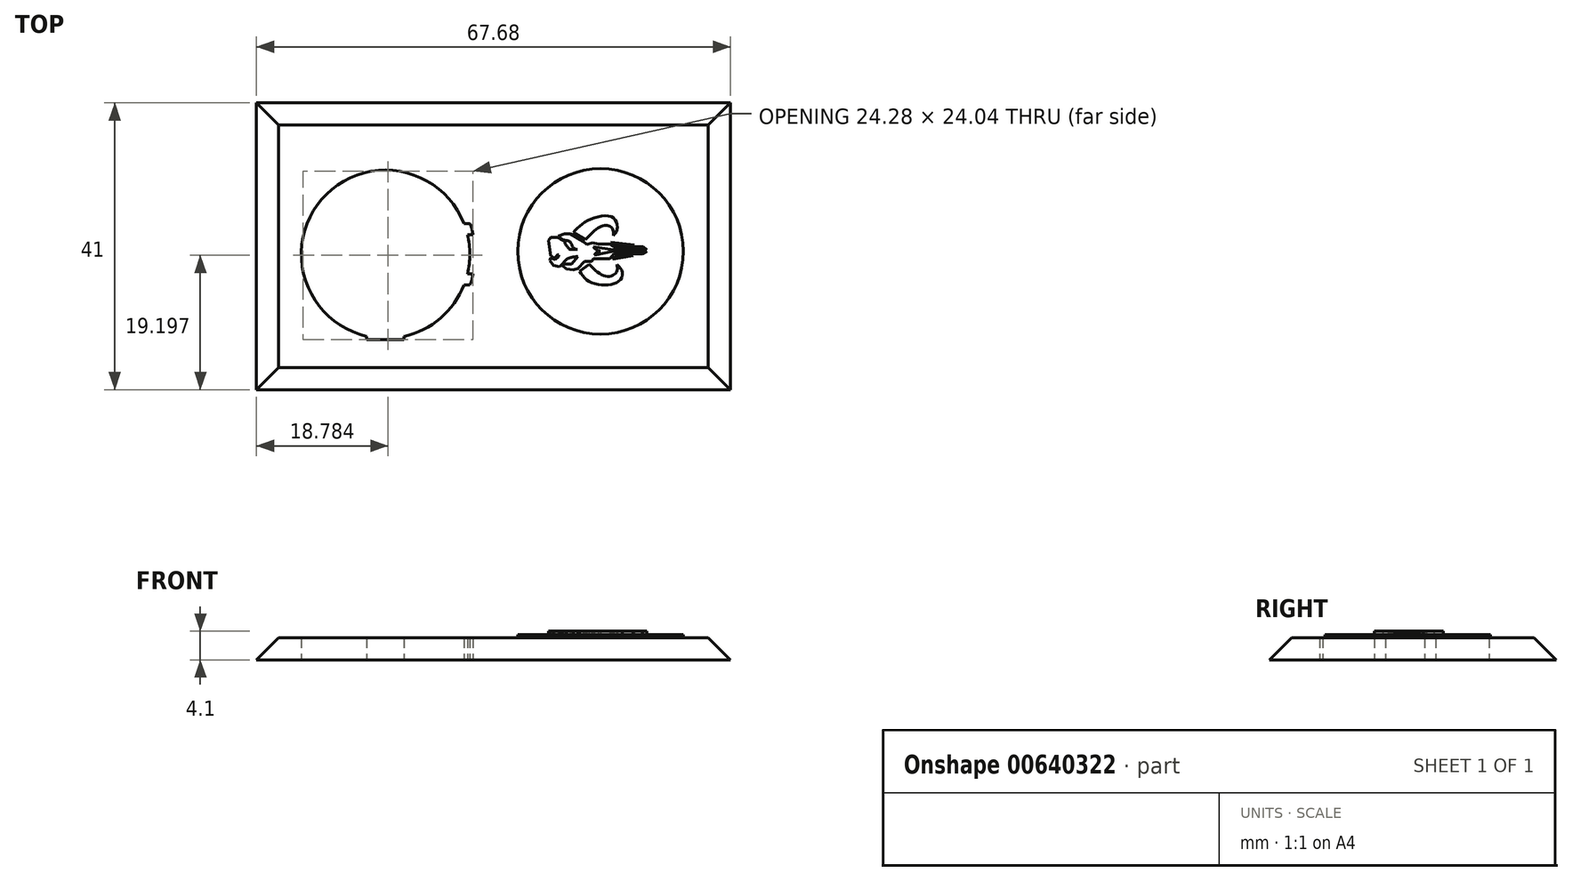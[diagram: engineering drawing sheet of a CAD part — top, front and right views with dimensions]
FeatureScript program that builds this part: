
annotation { "Feature Type Name" : "Feature", "Feature Type Description" : "" }
export const myFeature = defineFeature(function(context is Context, id is Id, definition is map)
    precondition{}
    {
        {
            var Q0;
            Q0=qCreatedBy(makeId("Top.planeOp"),FACE);
            var sketch = newSketch(context, id + "F0", { "sketchPlane" : qUnion([Q0])});
            skArc(sketch, "E0", {"start": v(2.63, -11.74) * mm, "mid": v(7.83, -9.13) * mm, "end": v(11.2, -4.38) * mm});
            skLineSegment(sketch, "E1.top", {"start": v(-2.68, -12.18) * mm, "end": v(2.63, -12.18) * mm});
            skLineSegment(sketch, "E1.left", {"start": v(-2.68, -11.73) * mm, "end": v(-2.68, -12.18) * mm});
            skLineSegment(sketch, "E1.right", {"start": v(2.63, -11.74) * mm, "end": v(2.63, -12.18) * mm});
            skArc(sketch, "E2", {"start": v(12.05, -4.38) * mm, "mid": v(12.31, -3.6) * mm, "end": v(12.49, -2.79) * mm});
            skLineSegment(sketch, "E3", {"start": v(12.05, -4.38) * mm, "end": v(11.2, -4.38) * mm});
            skLineSegment(sketch, "E4", {"start": v(12.49, -2.79) * mm, "end": v(11.7, -2.79) * mm});
            skArc(sketch, "E5.trimOffspring", {"start": v(11.7, -2.79) * mm, "mid": v(12.03, 0) * mm, "end": v(11.7, 2.79) * mm});
            skLineSegment(sketch, "E6.MirrorCS", {"start": v(12.05, 4.38) * mm, "end": v(11.2, 4.38) * mm});
            skLineSegment(sketch, "E7.MirrorCS", {"start": v(12.49, 2.79) * mm, "end": v(11.7, 2.79) * mm});
            skArc(sketch, "E8.MirrorCS", {"start": v(12.05, 4.38) * mm, "mid": v(12.31, 3.6) * mm, "end": v(12.49, 2.79) * mm});
            skArc(sketch, "E9.trimOffspring", {"start": v(11.2, 4.38) * mm, "mid": v(-9.11, 7.85) * mm, "end": v(-2.68, -11.73) * mm});
            skLineSegment(sketch, "E10.bottom", {"start": v(-18.44, -19.36) * mm, "end": v(49.24, -19.36) * mm});
            skLineSegment(sketch, "E10.top", {"start": v(-18.44, 21.64) * mm, "end": v(49.24, 21.64) * mm});
            skLineSegment(sketch, "E10.left", {"start": v(-18.44, -19.36) * mm, "end": v(-18.44, 21.64) * mm});
            skLineSegment(sketch, "E10.right", {"start": v(49.24, -19.36) * mm, "end": v(49.24, 21.64) * mm});
            skSolve(sketch);
        }
        {
            var Q0;
            Q0=makeQuery(id+"F0.imprint","IMPRINT",FACE,{"disambiguationData":[TD([[makeQuery(id+"F0.imprint","IMPRINT",EDGE,{"derivedFrom":sQuery(id+"F0.wireOp",EDGE,"E0")}),-1.0]])]});
            extrude(context, id + "F1", {"entities" : qUnion([Q0]), "depth" : 3.17 * mm, "offsetDistance" : 25 * mm});
        }
        {
            var Q0;
            Q0=makeQuery(id+"F0.imprint","IMPRINT",FACE,{"disambiguationData":[TD([[makeQuery(id+"F0.imprint","IMPRINT",EDGE,{"derivedFrom":sQuery(id+"F0.wireOp",EDGE,"E0")}),1.0]])]});
            extrude(context, id + "F2", {"entities" : qUnion([Q0]), "depth" : 1 / 406.4 * mm, "offsetDistance" : 25 * mm});
        }
        {
            var Q0;
            Q0=qCreatedBy(makeId("Top.planeOp"),FACE);
            var sketch = newSketch(context, id + "F3", { "sketchPlane" : qUnion([Q0])});
            skCircle(sketch, "E11", {"center": v(30.7, 0.41) * mm, "radius": 11.82 * mm});
            skPoint(sketch, "E11.first.point", {"position": v(42.5, 0.04) * mm});
            skPoint(sketch, "E11.second.point", {"position": v(18.88, 0.85) * mm});
            skPoint(sketch, "E11.third.point", {"position": v(31.83, 12.18) * mm});
            skFitSpline(sketch, "E12", {"points": [v(27.7, -2.4) * mm, v(28.93, -3.83) * mm, v(31.38, -4.38) * mm, v(33.21, -3.9) * mm, v(33.83, -2.68) * mm, v(33.01, -1.45) * mm], "startDerivative": vector(4.86, -7.94) * mm, "endDerivative": vector(-6.38, 6.46) * mm});
            skFitSpline(sketch, "E13", {"points": [v(33.01, -1.45) * mm, v(33.01, -2.47) * mm, v(31.99, -3.15) * mm, v(30.15, -2.47) * mm, v(29.06, -1.45) * mm, v(29, -1.45) * mm], "startDerivative": vector(1.04, -5.28) * mm, "endDerivative": vector(-1.05, -0.42) * mm});
            skLineSegment(sketch, "E14", {"start": v(27.7, -2.4) * mm, "end": v(29.01, -1.44) * mm});
            skFitSpline(sketch, "E15", {"points": [v(25.8, 1.98) * mm, v(26.37, 1.74) * mm, v(26.8, 0.94) * mm, v(27.4, 0.67) * mm], "startDerivative": vector(2.1, -0.35) * mm, "endDerivative": vector(2.16, -0.43) * mm});
            skLineSegment(sketch, "E16", {"start": v(27.4, 0.67) * mm, "end": v(26.32, 0.67) * mm});
            skFitSpline(sketch, "E17", {"points": [v(26.32, 0.67) * mm, v(25.59, 1.65) * mm, v(25.58, 1.79) * mm, v(24.54, 2.4) * mm], "startDerivative": vector(-2.44, 2.83) * mm, "endDerivative": vector(-3.42, 1.68) * mm});
            skFitSpline(sketch, "E18", {"points": [v(25.8, 1.98) * mm, v(25.24, 2.12) * mm, v(24.64, 2.57) * mm], "startDerivative": vector(-1.19, 0.2) * mm, "endDerivative": vector(-1.12, 0.97) * mm});
            skFitSpline(sketch, "E19", {"points": [v(25.95, -0.65) * mm, v(26.58, -0.43) * mm, v(27.47, -0.33) * mm], "startDerivative": vector(1.28, 0.55) * mm, "endDerivative": vector(1.74, 0.1) * mm});
            skLineSegment(sketch, "E20", {"start": v(27.47, -0.33) * mm, "end": v(26.54, -1.4) * mm});
            skLineSegment(sketch, "E21", {"start": v(26.54, -1.4) * mm, "end": v(25.37, -1.4) * mm});
            skLineSegment(sketch, "E22", {"start": v(25.37, -1.4) * mm, "end": v(25.2, -1.62) * mm});
            skLineSegment(sketch, "E23", {"start": v(25.95, -0.65) * mm, "end": v(24.83, -1.75) * mm});
            skLineSegment(sketch, "E24", {"start": v(25.2, -1.62) * mm, "end": v(25.84, -2.11) * mm});
            skLineSegment(sketch, "E25", {"start": v(25.84, -2.11) * mm, "end": v(26.83, -2.23) * mm});
            skLineSegment(sketch, "E26", {"start": v(26.83, -2.23) * mm, "end": v(27.47, -2.04) * mm});
            skLineSegment(sketch, "E27", {"start": v(27.47, -2.04) * mm, "end": v(28.42, -1.02) * mm});
            skLineSegment(sketch, "E28", {"start": v(28.42, -1.02) * mm, "end": v(29.4, -1.02) * mm});
            skLineSegment(sketch, "E29", {"start": v(29.4, -1.02) * mm, "end": v(29.69, -0.65) * mm});
            skLineSegment(sketch, "E30", {"start": v(29.69, -0.65) * mm, "end": v(32.02, -0.65) * mm});
            skLineSegment(sketch, "E31", {"start": v(32.02, -0.65) * mm, "end": v(32.6, 0.07) * mm});
            skLineSegment(sketch, "E32", {"start": v(32.6, 0.07) * mm, "end": v(36.69, 0.07) * mm});
            skLineSegment(sketch, "E33", {"start": v(36.69, 0.07) * mm, "end": v(37.3, 0.41) * mm});
            skLineSegment(sketch, "E34", {"start": v(37.3, 0.41) * mm, "end": v(32.53, 0.41) * mm});
            skLineSegment(sketch, "E35", {"start": v(32.53, 0.41) * mm, "end": v(29.83, -0.13) * mm});
            skLineSegment(sketch, "E36", {"start": v(37.3, 0.66) * mm, "end": v(36.78, 1.06) * mm});
            skLineSegment(sketch, "E37", {"start": v(36.78, 1.06) * mm, "end": v(32.5, 1.06) * mm});
            skLineSegment(sketch, "E38", {"start": v(32.5, 1.06) * mm, "end": v(32.02, 1.44) * mm});
            skLineSegment(sketch, "E39", {"start": v(32.02, 1.44) * mm, "end": v(30.39, 1.44) * mm});
            skLineSegment(sketch, "E40", {"start": v(30.39, 1.44) * mm, "end": v(29.54, 1.65) * mm});
            skLineSegment(sketch, "E41", {"start": v(29.54, 1.65) * mm, "end": v(28.75, 1.4) * mm});
            skLineSegment(sketch, "E42", {"start": v(28.75, 1.4) * mm, "end": v(28.22, 1.82) * mm});
            skLineSegment(sketch, "E43", {"start": v(28.22, 1.82) * mm, "end": v(26.37, 2.9) * mm});
            skLineSegment(sketch, "E44", {"start": v(26.37, 2.9) * mm, "end": v(25.55, 2.9) * mm});
            skLineSegment(sketch, "E45", {"start": v(25.55, 2.9) * mm, "end": v(24.64, 2.57) * mm});
            skLineSegment(sketch, "E46", {"start": v(24.54, 2.4) * mm, "end": v(23.6, 2.4) * mm});
            skLineSegment(sketch, "E47", {"start": v(23.6, 2.4) * mm, "end": v(23.27, 1.98) * mm});
            skLineSegment(sketch, "E48", {"start": v(23.27, 1.98) * mm, "end": v(23.56, -0.24) * mm});
            skLineSegment(sketch, "E49", {"start": v(23.56, -0.24) * mm, "end": v(24.14, -0.57) * mm});
            skLineSegment(sketch, "E50", {"start": v(24.14, -0.57) * mm, "end": v(24.56, -0.04) * mm});
            skLineSegment(sketch, "E51", {"start": v(24.56, -0.04) * mm, "end": v(24.6, -0.07) * mm});
            skLineSegment(sketch, "E52", {"start": v(24.6, -0.07) * mm, "end": v(24.75, -0.07) * mm});
            skLineSegment(sketch, "E53", {"start": v(24.75, -0.07) * mm, "end": v(24.64, -0.38) * mm});
            skLineSegment(sketch, "E54", {"start": v(24.64, -0.38) * mm, "end": v(24.24, -0.78) * mm});
            skLineSegment(sketch, "E55", {"start": v(24.24, -0.78) * mm, "end": v(23.6, -0.5) * mm});
            skLineSegment(sketch, "E56", {"start": v(23.6, -0.5) * mm, "end": v(23.43, -0.9) * mm});
            skLineSegment(sketch, "E57", {"start": v(23.43, -0.9) * mm, "end": v(23.97, -1.62) * mm});
            skLineSegment(sketch, "E58", {"start": v(23.97, -1.62) * mm, "end": v(24.83, -1.75) * mm});
            skLineSegment(sketch, "E59", {"start": v(37.3, 0.66) * mm, "end": v(32.5, 0.66) * mm});
            skLineSegment(sketch, "E60", {"start": v(32.5, 0.66) * mm, "end": v(29.66, 1.06) * mm});
            skArc(sketch, "E61", {"start": v(29.66, 1.06) * mm, "mid": v(30.12, 0.64) * mm, "end": v(30.7, 0.41) * mm});
            skArc(sketch, "E62", {"start": v(30.7, 0.41) * mm, "mid": v(30.17, 0.28) * mm, "end": v(29.83, -0.13) * mm});
            skFitSpline(sketch, "E63", {"points": [v(28.5, 2.09) * mm, v(30.65, 3.91) * mm, v(31.8, 4.08) * mm, v(32.45, 3.55) * mm, v(32.5, 2.64) * mm], "startDerivative": vector(6.13, 6.16) * mm, "endDerivative": vector(-0.5, -4.73) * mm});
            skFitSpline(sketch, "E64", {"points": [v(32.5, 2.64) * mm, v(33.05, 3.53) * mm, v(32.5, 5.21) * mm, v(29.18, 4.97) * mm, v(26.8, 3.1) * mm], "startDerivative": vector(4.04, 4.24) * mm, "endDerivative": vector(-6.84, -7.14) * mm});
            skLineSegment(sketch, "E65", {"start": v(28.5, 2.09) * mm, "end": v(26.8, 3.1) * mm});
            skLineSegment(sketch, "E66", {"start": v(32.4, -0.7) * mm, "end": v(32.96, -0.22) * mm});
            skLineSegment(sketch, "E67", {"start": v(32.96, -0.22) * mm, "end": v(35.32, -0.22) * mm});
            skLineSegment(sketch, "E68", {"start": v(35.32, -0.22) * mm, "end": v(32.4, -0.7) * mm});
            skLineSegment(sketch, "E69", {"start": v(32.6, 1.34) * mm, "end": v(35.5, 1.34) * mm});
            skLineSegment(sketch, "E70", {"start": v(35.5, 1.34) * mm, "end": v(32.16, 1.7) * mm});
            skLineSegment(sketch, "E71", {"start": v(32.16, 1.7) * mm, "end": v(32.6, 1.34) * mm});
            skSolve(sketch);
        }
        {
            var Q0;
            Q0=makeQuery(id+"F3.imprint","IMPRINT",FACE,{"disambiguationData":[TD([[makeQuery(id+"F3.imprint","IMPRINT",EDGE,{"derivedFrom":sQuery(id+"F3.wireOp",EDGE,"E11")}),1.0]])]});
            extrude(context, id + "F4", {"entities" : qUnion([Q0]), "operationType" : NewBodyOperationType.ADD, "depth" : 3.6 * mm, "offsetDistance" : 25 * mm});
        }
        {
            var Q0;
            Q0=makeQuery(id+"F3.imprint","IMPRINT",FACE,{"disambiguationData":[TD([[makeQuery(id+"F3.imprint","IMPRINT",EDGE,{"derivedFrom":sQuery(id+"F3.wireOp",EDGE,"E15")}),1.0]])]});
            var Q1;
            {var subQ0=sQuery(id+"F3.wireOp",EDGE,"E12");Q1=makeQuery(id+"F3.imprint","IMPRINT",FACE,{"disambiguationData":[TD([[makeQuery(id+"F3.imprint","IMPRINT",EDGE,{"derivedFrom":subQ0}),1.0]])]});}
            var Q2;
            Q2=makeQuery(id+"F3.imprint","IMPRINT",FACE,{"disambiguationData":[TD([[makeQuery(id+"F3.imprint","IMPRINT",EDGE,{"derivedFrom":sQuery(id+"F3.wireOp",EDGE,"E63")}),1.0]])]});
            var Q3;
            Q3=makeQuery(id+"F3.imprint","IMPRINT",FACE,{"disambiguationData":[TD([[makeQuery(id+"F3.imprint","IMPRINT",EDGE,{"derivedFrom":sQuery(id+"F3.wireOp",EDGE,"E69")}),1.0]])]});
            var Q4;
            Q4=makeQuery(id+"F3.imprint","IMPRINT",FACE,{"disambiguationData":[TD([[makeQuery(id+"F3.imprint","IMPRINT",EDGE,{"derivedFrom":sQuery(id+"F3.wireOp",EDGE,"E66")}),-1.0]])]});
            extrude(context, id + "F5", {"entities" : qUnion([Q0, Q1, Q2, Q3, Q4]), "operationType" : NewBodyOperationType.ADD, "depth" : 4.1 * mm, "offsetDistance" : 25 * mm});
        }
        {
            var Q0;
            Q0=makeQuery(id+"F1.opExtrude","CAP_EDGE",EDGE,{"disambiguationData":[OSD([sQuery(id+"F0.wireOp",EDGE,"E10.right")])],"isStart":false});
            var Q1;
            Q1=makeQuery(id+"F1.opExtrude","CAP_EDGE",EDGE,{"disambiguationData":[OSD([sQuery(id+"F0.wireOp",EDGE,"E10.bottom")])],"isStart":false});
            var Q2;
            Q2=makeQuery(id+"F1.opExtrude","CAP_EDGE",EDGE,{"disambiguationData":[OSD([sQuery(id+"F0.wireOp",EDGE,"E10.left")])],"isStart":false});
            var Q3;
            Q3=makeQuery(id+"F1.opExtrude","CAP_EDGE",EDGE,{"disambiguationData":[OSD([sQuery(id+"F0.wireOp",EDGE,"E10.top")])],"isStart":false});
            chamfer(context, id + "F6", {"entities" : qUnion([Q0, Q1, Q2, Q3]), "width" : 3.17 * mm, "tangentPropagation" : true});
        }
    });
